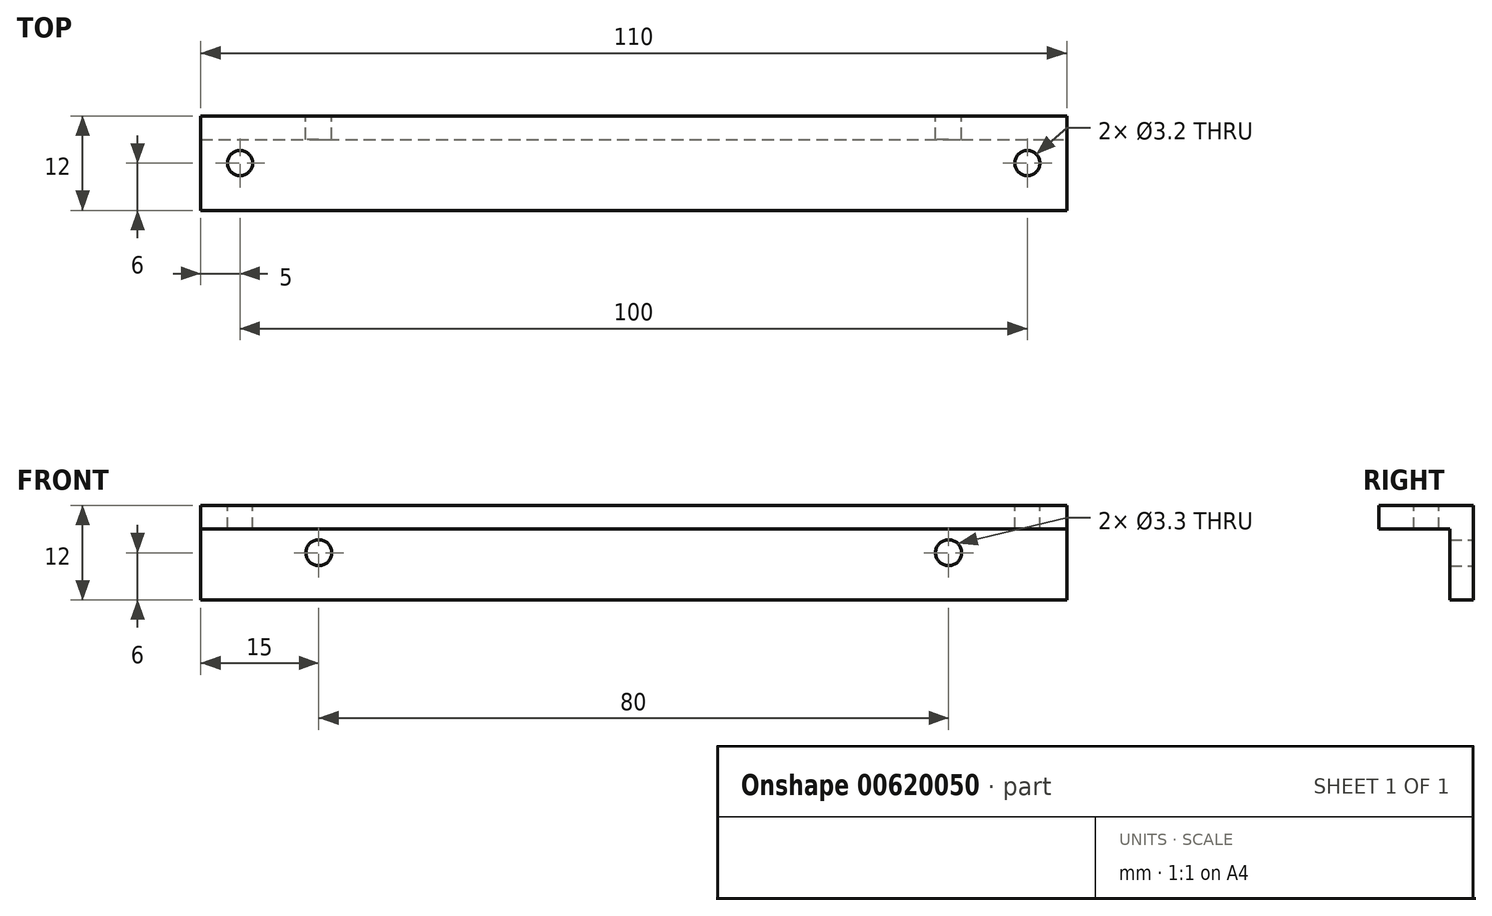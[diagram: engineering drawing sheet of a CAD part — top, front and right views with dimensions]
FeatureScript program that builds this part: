
annotation { "Feature Type Name" : "Feature", "Feature Type Description" : "" }
export const myFeature = defineFeature(function(context is Context, id is Id, definition is map)
    precondition{}
    {
        {
            var Q0;
            Q0=qCreatedBy(makeId("Right.planeOp"),FACE);
            var sketch = newSketch(context, id + "F0", { "sketchPlane" : qUnion([Q0])});
            skLineSegment(sketch, "E0", {"start": v(0, 0) * mm, "end": v(-12, 0) * mm});
            skLineSegment(sketch, "E1", {"start": v(-12, 0) * mm, "end": v(-12, 3) * mm});
            skLineSegment(sketch, "E2", {"start": v(-12, 3) * mm, "end": v(-3, 3) * mm});
            skLineSegment(sketch, "E3", {"start": v(-3, 3) * mm, "end": v(-3, 12) * mm});
            skLineSegment(sketch, "E4", {"start": v(-3, 12) * mm, "end": v(0, 12) * mm});
            skLineSegment(sketch, "E5", {"start": v(0, 12) * mm, "end": v(0, 0) * mm});
            skSolve(sketch);
        }
        {
            var Q0;
            Q0=makeQuery(id+"F0.imprint","IMPRINT",FACE,{"disambiguationData":[TD([[makeQuery(id+"F0.imprint","IMPRINT",EDGE,{"derivedFrom":sQuery(id+"F0.wireOp",EDGE,"E0")}),-1.0]])]});
            extrude(context, id + "F1", {"entities" : qUnion([Q0]), "endBound" : BoundingType.SYMMETRIC, "depth" : 110 * mm, "offsetDistance" : 25 * mm});
        }
        {
            var Q0;
            Q0=makeQuery(id+"F1.opExtrude","SWEPT_FACE",FACE,{"disambiguationData":[OSD([sQuery(id+"F0.wireOp",EDGE,"E0")])]});
            var sketch = newSketch(context, id + "F2", { "sketchPlane" : qUnion([Q0])});
            skLineSegment(sketch, "E6", {"start": v(0, 0) * mm, "end": v(0, 12) * mm, "construction": true});
            skLineSegment(sketch, "E7", {"start": v(-55, 6) * mm, "end": v(55, 6) * mm, "construction": true});
            skPoint(sketch, "E8", {"position": v(-50, 6) * mm});
            skPoint(sketch, "E9.MirrorP", {"position": v(50, 6) * mm});
            skSolve(sketch);
        }
        {
            var Q0;
            Q0=sQuery(id+"F2.wireOp",VERTEX,"E8");
            var Q1;
            Q1=sQuery(id+"F2.wireOp",VERTEX,"E9.MirrorP");
            var Q2;
            Q2=makeQuery(id+"F1.opExtrude","SWEPT_BODY",BODY,{"disambiguationData":[OSD([sQuery(id+"F0.wireOp",EDGE,"E0"),sQuery(id+"F0.wireOp",EDGE,"E1"),sQuery(id+"F0.wireOp",EDGE,"E2"),sQuery(id+"F0.wireOp",EDGE,"E3"),sQuery(id+"F0.wireOp",EDGE,"E4"),sQuery(id+"F0.wireOp",EDGE,"E5")])]});
            hole(context, id + "F3", {"style" : HoleStyle.SIMPLE, "endStyle" : HoleEndStyle.THROUGH, "standardTappedOrClearance" : lookupTablePath({ "standard" : "ISO", "engagement" : "75%", "pitch" : "0.75 mm", "size" : "M4", "type" : "Tapped" }), "standardBlindInLast" : lookupTablePath({ "standard" : "ISO", "engagement" : "75%", "pitch" : "0.75 mm", "size" : "M4", "type" : "Tapped" }), "holeDiameter" : 3.2 * mm, "majorDiameter" : 5 * mm, "showTappedDepth" : true, "isTappedThrough" : true, "tappedDepth" : 12 * mm, "tapClearance" : 3, "locations" : qUnion([Q0, Q1]), "scope" : qUnion([Q2])});
        }
        {
            var Q0;
            Q0=makeQuery(id+"F1.opExtrude","SWEPT_FACE",FACE,{"disambiguationData":[OSD([sQuery(id+"F0.wireOp",EDGE,"E5")])]});
            var sketch = newSketch(context, id + "F4", { "sketchPlane" : qUnion([Q0])});
            skLineSegment(sketch, "E10", {"start": v(0, 0) * mm, "end": v(0, 12) * mm, "construction": true});
            skLineSegment(sketch, "E11", {"start": v(55, 6) * mm, "end": v(-55, 6) * mm, "construction": true});
            skPoint(sketch, "E12", {"position": v(40, 6) * mm});
            skPoint(sketch, "E13.MirrorP", {"position": v(-40, 6) * mm});
            skSolve(sketch);
        }
        {
            var Q0;
            Q0=sQuery(id+"F4.wireOp",VERTEX,"E12");
            var Q1;
            Q1=sQuery(id+"F4.wireOp",VERTEX,"E13.MirrorP");
            var Q2;
            Q2=makeQuery(id+"F1.opExtrude","SWEPT_BODY",BODY,{"disambiguationData":[OSD([sQuery(id+"F0.wireOp",EDGE,"E0"),sQuery(id+"F0.wireOp",EDGE,"E1"),sQuery(id+"F0.wireOp",EDGE,"E2"),sQuery(id+"F0.wireOp",EDGE,"E3"),sQuery(id+"F0.wireOp",EDGE,"E4"),sQuery(id+"F0.wireOp",EDGE,"E5")])]});
            hole(context, id + "F5", {"style" : HoleStyle.SIMPLE, "endStyle" : HoleEndStyle.THROUGH, "standardTappedOrClearance" : lookupTablePath({ "standard" : "ISO", "engagement" : "75%", "pitch" : "0.7 mm", "size" : "M4", "type" : "Tapped" }), "standardBlindInLast" : lookupTablePath({ "standard" : "ISO", "engagement" : "75%", "pitch" : "0.7 mm", "size" : "M4", "type" : "Tapped" }), "holeDiameter" : 3.3 * mm, "majorDiameter" : 4 * mm, "showTappedDepth" : true, "isTappedThrough" : true, "tappedDepth" : 12 * mm, "tapClearance" : 3, "locations" : qUnion([Q0, Q1]), "scope" : qUnion([Q2])});
        }
        {
            var Q0;
            Q0=makeQuery(id+"F1.opExtrude","SWEPT_BODY",BODY,{"disambiguationData":[OSD([sQuery(id+"F0.wireOp",EDGE,"E0"),sQuery(id+"F0.wireOp",EDGE,"E1"),sQuery(id+"F0.wireOp",EDGE,"E2"),sQuery(id+"F0.wireOp",EDGE,"E3"),sQuery(id+"F0.wireOp",EDGE,"E4"),sQuery(id+"F0.wireOp",EDGE,"E5")])]});
            var Q1;
            Q1=makeQuery(id+"F1.opExtrude","SWEPT_EDGE",EDGE,{"disambiguationData":[OSD([sQuery(id+"F0.wireOp",EDGE,"E0"),sQuery(id+"F0.wireOp",EDGE,"E5")])]});
            transform(context, id + "F6", {"entities" : qUnion([Q0]), "transformType" : TransformType.ROTATION, "transformAxis" : qUnion([Q1]), "angle" : 180 * degree, "oppositeDirection" : true, "makeCopy" : false});
        }
        {
            var Q0;
            Q0=makeQuery(id+"F1.opExtrude","SWEPT_FACE",FACE,{"disambiguationData":[OSD([sQuery(id+"F0.wireOp",EDGE,"E5")])]});
            var sketch = newSketch(context, id + "F7", { "sketchPlane" : qUnion([Q0])});
            skLineSegment(sketch, "E14", {"start": v(0, 0) * mm, "end": v(0, 34.26) * mm, "construction": true});
            skSolve(sketch);
        }
        {
            var Q0;
            Q0=makeQuery(id+"F1.opExtrude","SWEPT_BODY",BODY,{"disambiguationData":[OSD([sQuery(id+"F0.wireOp",EDGE,"E0"),sQuery(id+"F0.wireOp",EDGE,"E1"),sQuery(id+"F0.wireOp",EDGE,"E2"),sQuery(id+"F0.wireOp",EDGE,"E3"),sQuery(id+"F0.wireOp",EDGE,"E4"),sQuery(id+"F0.wireOp",EDGE,"E5")])]});
            var Q1;
            Q1=sQuery(id+"F7.wireOp",EDGE,"E14");
            transform(context, id + "F8", {"entities" : qUnion([Q0]), "transformType" : TransformType.ROTATION, "transformAxis" : qUnion([Q1]), "angle" : 180 * degree, "makeCopy" : false});
        }
    });
